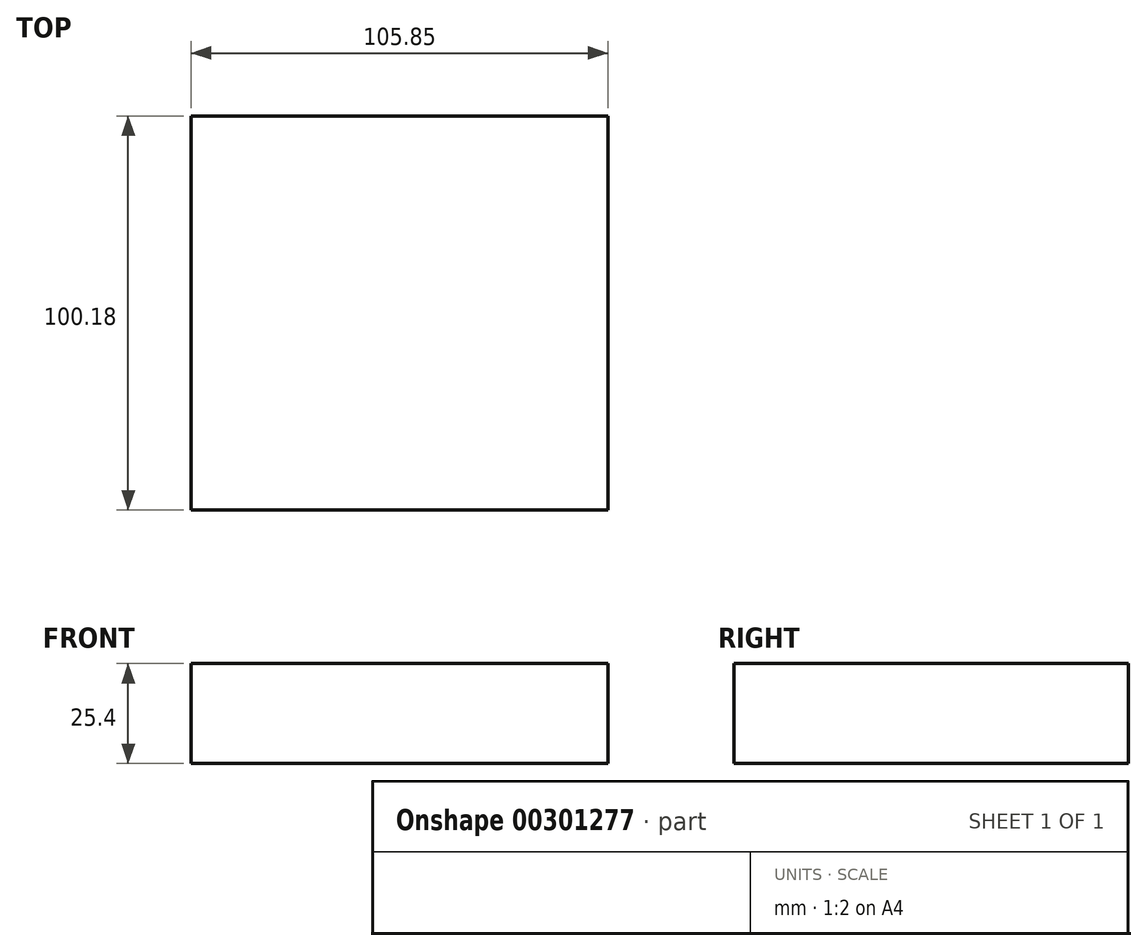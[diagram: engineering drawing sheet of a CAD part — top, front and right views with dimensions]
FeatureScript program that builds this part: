
annotation { "Feature Type Name" : "Feature", "Feature Type Description" : "" }
export const myFeature = defineFeature(function(context is Context, id is Id, definition is map)
    precondition{}
    {
        {
            var Q0;
            Q0=qCreatedBy(makeId("Top.planeOp"),FACE);
            var sketch = newSketch(context, id + "F0", { "sketchPlane" : qUnion([Q0])});
            skLineSegment(sketch, "E0.bottom", {"start": v(0, 0) * mm, "end": v(-105.85, 0) * mm});
            skLineSegment(sketch, "E0.top", {"start": v(0, -100.18) * mm, "end": v(-105.85, -100.18) * mm});
            skLineSegment(sketch, "E0.left", {"start": v(0, 0) * mm, "end": v(0, -100.18) * mm});
            skLineSegment(sketch, "E0.right", {"start": v(-105.85, 0) * mm, "end": v(-105.85, -100.18) * mm});
            skSolve(sketch);
        }
        {
            var Q0;
            Q0 = qSketchRegion(id + "F0", true);
            extrude(context, id + "F1", {"entities" : qUnion([Q0]), "depth" : 25.4 * mm});
        }
    });
